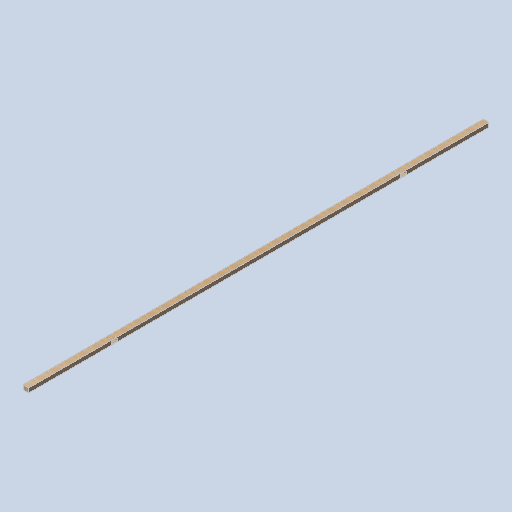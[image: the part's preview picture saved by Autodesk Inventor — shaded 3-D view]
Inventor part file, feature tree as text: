
AUTODESK INVENTOR PART (.ipt)
format: ipt  version: 2024.2 (Build 282272000, 272)  size: 106,496 bytes
history: native  units: in
note: dims shown in document units (in); Inventor stores cm internally (conversion verified against a paired STEP export)
features: other x3, sketch x2
ambient origin geometry x8: Origin, YZ Plane, XZ Plane, XY Plane, X Axis, Y Axis, Z Axis, Center Point
bodies: Solid1 (feature_tree)
feature tree (5):
  other  "support_frame_01.ipt"
  other  "Solid1::support_frame_01.ipt"
  other  "TaggingFeature1"
  sketch  "Sketch1"  dims[d0=0.3937in]
  sketch  "Sketch2"
